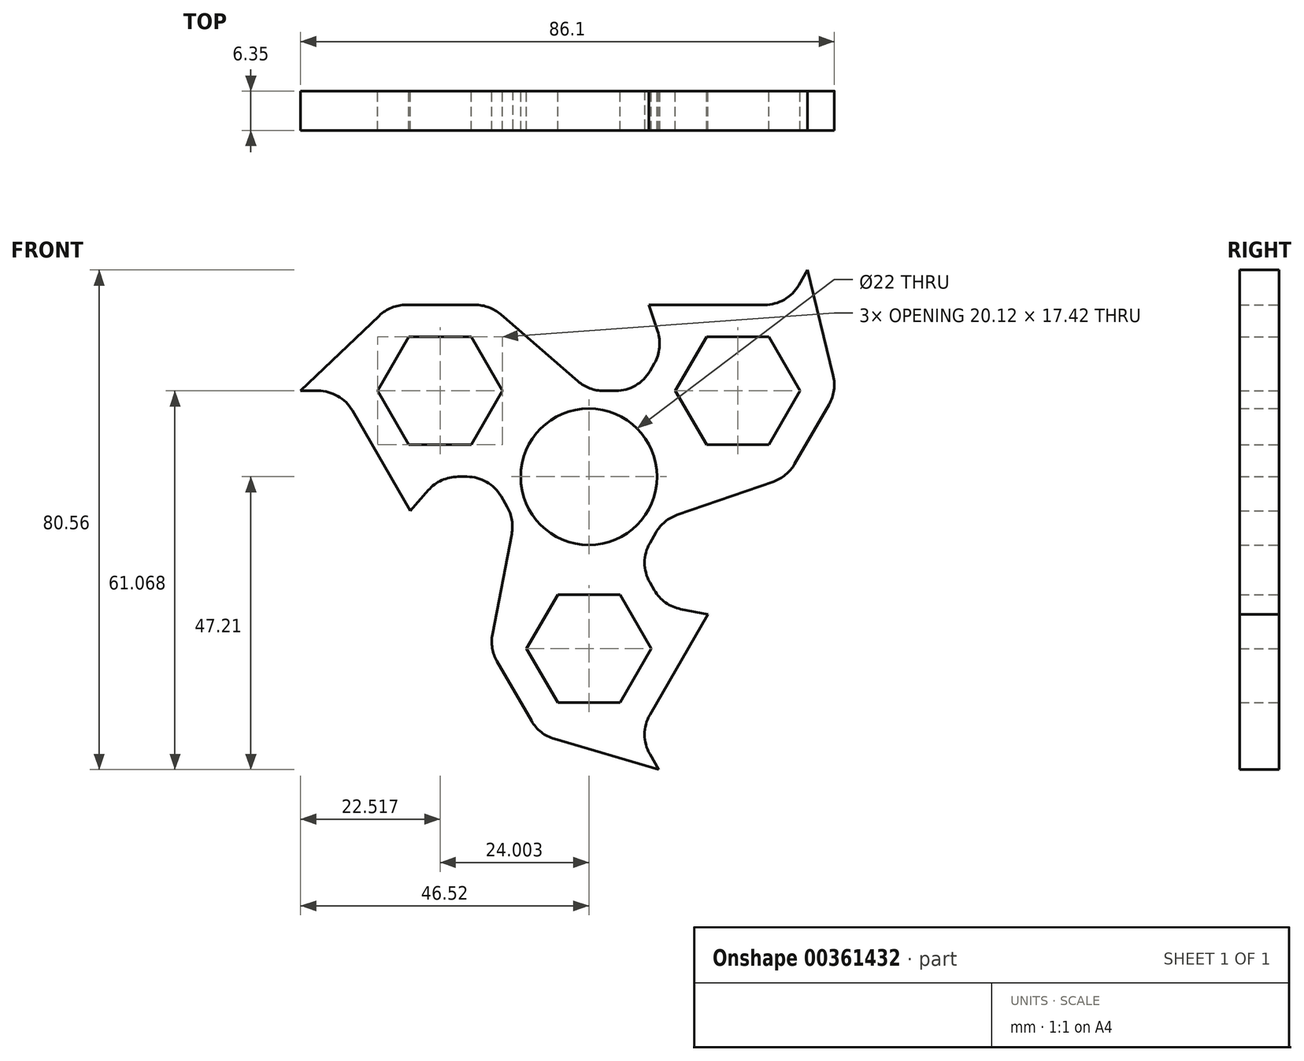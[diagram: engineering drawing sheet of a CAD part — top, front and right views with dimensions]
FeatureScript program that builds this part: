
annotation { "Feature Type Name" : "Feature", "Feature Type Description" : "" }
export const myFeature = defineFeature(function(context is Context, id is Id, definition is map)
    precondition{}
    {
        {
            var Q0;
            Q0=qCreatedBy(makeId("Front.planeOp"),FACE);
            var sketch = newSketch(context, id + "F0", { "sketchPlane" : qUnion([Q0])});
            skCircle(sketch, "E0.cCircle", {"center": v(0, 0) * mm, "radius": 13.86 * mm, "construction": true});
            skLineSegment(sketch, "E0.0", {"start": v(8, -13.86) * mm, "end": v(-8, -13.86) * mm});
            skLineSegment(sketch, "E0.1", {"start": v(-8, -13.86) * mm, "end": v(-16, 0) * mm});
            skLineSegment(sketch, "E0.2", {"start": v(-16, 0) * mm, "end": v(-8, 13.86) * mm});
            skLineSegment(sketch, "E0.3", {"start": v(-8, 13.86) * mm, "end": v(8, 13.86) * mm});
            skLineSegment(sketch, "E0.4", {"start": v(8, 13.86) * mm, "end": v(16, 0) * mm});
            skLineSegment(sketch, "E0.5", {"start": v(16, 0) * mm, "end": v(8, -13.86) * mm});
            skPoint(sketch, "E0.0.midPoint", {"position": v(0, -13.86) * mm});
            skCircle(sketch, "E1.cCircle", {"center": v(-24, 13.86) * mm, "radius": 13.86 * mm, "construction": true});
            skLineSegment(sketch, "E1.0", {"start": v(-16, 0) * mm, "end": v(-32, 0) * mm});
            skLineSegment(sketch, "E1.1", {"start": v(-32, 0) * mm, "end": v(-40, 13.86) * mm});
            skLineSegment(sketch, "E1.2", {"start": v(-40, 13.86) * mm, "end": v(-32, 27.72) * mm});
            skLineSegment(sketch, "E1.3", {"start": v(-32, 27.72) * mm, "end": v(-16, 27.72) * mm});
            skLineSegment(sketch, "E1.4", {"start": v(-16, 27.72) * mm, "end": v(-8, 13.86) * mm});
            skLineSegment(sketch, "E1.5", {"start": v(-8, 13.86) * mm, "end": v(-16, 0) * mm});
            skPoint(sketch, "E1.0.midPoint", {"position": v(-24, 0) * mm});
            skCircle(sketch, "E2", {"center": v(0, 0) * mm, "radius": 11 * mm});
            skCircle(sketch, "E3.cCircle", {"center": v(-24, 13.86) * mm, "radius": 8.71 * mm, "construction": true});
            skLineSegment(sketch, "E3.0", {"start": v(-18.97, 5.15) * mm, "end": v(-29.03, 5.15) * mm});
            skLineSegment(sketch, "E3.1", {"start": v(-29.03, 5.15) * mm, "end": v(-34.06, 13.86) * mm});
            skLineSegment(sketch, "E3.2", {"start": v(-34.06, 13.86) * mm, "end": v(-29.03, 22.57) * mm});
            skLineSegment(sketch, "E3.3", {"start": v(-29.03, 22.57) * mm, "end": v(-18.97, 22.57) * mm});
            skLineSegment(sketch, "E3.4", {"start": v(-18.97, 22.57) * mm, "end": v(-13.94, 13.86) * mm});
            skLineSegment(sketch, "E3.5", {"start": v(-13.94, 13.86) * mm, "end": v(-18.97, 5.15) * mm});
            skPoint(sketch, "E3.0.midPoint", {"position": v(-24, 5.15) * mm});
            skLineSegment(sketch, "E4.1.2", {"start": v(8, -41.57) * mm, "end": v(-8, -41.57) * mm});
            skCircle(sketch, "E4.1.3", {"center": v(0, -27.72) * mm, "radius": 13.86 * mm, "construction": true});
            skLineSegment(sketch, "E4.1.4", {"start": v(-16, -27.72) * mm, "end": v(-8, -13.86) * mm});
            skLineSegment(sketch, "E4.1.6", {"start": v(8, -13.86) * mm, "end": v(16, -27.72) * mm});
            skLineSegment(sketch, "E4.1.7", {"start": v(-5.03, -36.43) * mm, "end": v(-10.06, -27.72) * mm});
            skCircle(sketch, "E4.1.8", {"center": v(0, -27.72) * mm, "radius": 8.71 * mm, "construction": true});
            skLineSegment(sketch, "E4.1.9", {"start": v(5.03, -36.43) * mm, "end": v(-5.03, -36.43) * mm});
            skLineSegment(sketch, "E4.1.10", {"start": v(10.06, -27.72) * mm, "end": v(5.03, -36.43) * mm});
            skLineSegment(sketch, "E4.1.11", {"start": v(5.03, -19) * mm, "end": v(10.06, -27.72) * mm});
            skLineSegment(sketch, "E4.1.12", {"start": v(-5.03, -19) * mm, "end": v(5.03, -19) * mm});
            skLineSegment(sketch, "E4.2.2", {"start": v(32, 27.72) * mm, "end": v(40, 13.86) * mm});
            skCircle(sketch, "E4.2.3", {"center": v(24, 13.86) * mm, "radius": 13.86 * mm, "construction": true});
            skLineSegment(sketch, "E4.2.4", {"start": v(32, 0) * mm, "end": v(16, 0) * mm});
            skLineSegment(sketch, "E4.2.6", {"start": v(8, 13.86) * mm, "end": v(16, 27.72) * mm});
            skLineSegment(sketch, "E4.2.7", {"start": v(34.06, 13.86) * mm, "end": v(29.03, 5.15) * mm});
            skCircle(sketch, "E4.2.8", {"center": v(24, 13.86) * mm, "radius": 8.71 * mm, "construction": true});
            skLineSegment(sketch, "E4.2.9", {"start": v(29.03, 22.57) * mm, "end": v(34.06, 13.86) * mm});
            skLineSegment(sketch, "E4.2.10", {"start": v(18.97, 22.57) * mm, "end": v(29.03, 22.57) * mm});
            skLineSegment(sketch, "E4.2.11", {"start": v(13.94, 13.86) * mm, "end": v(18.97, 22.57) * mm});
            skLineSegment(sketch, "E4.2.12", {"start": v(18.97, 5.15) * mm, "end": v(13.94, 13.86) * mm});
            skLineSegment(sketch, "E5", {"start": v(-32, 0) * mm, "end": v(-28.83, -5.5) * mm});
            skLineSegment(sketch, "E6", {"start": v(-28.83, -5.5) * mm, "end": v(-24, 0) * mm});
            skLineSegment(sketch, "E7.1.0", {"start": v(16, -27.72) * mm, "end": v(19.18, -22.22) * mm});
            skLineSegment(sketch, "E7.1.1", {"start": v(19.18, -22.22) * mm, "end": v(12, -20.79) * mm});
            skLineSegment(sketch, "E7.2.0", {"start": v(16, 27.72) * mm, "end": v(9.65, 27.72) * mm});
            skLineSegment(sketch, "E7.2.1", {"start": v(9.65, 27.72) * mm, "end": v(12, 20.79) * mm});
            skLineSegment(sketch, "E8.1.0", {"start": v(-10.06, -27.72) * mm, "end": v(-5.03, -19) * mm});
            skLineSegment(sketch, "E8.2.0", {"start": v(29.03, 5.15) * mm, "end": v(18.97, 5.15) * mm});
            skLineSegment(sketch, "E9", {"start": v(16, 27.72) * mm, "end": v(32, 27.72) * mm});
            skLineSegment(sketch, "E10", {"start": v(40, 13.86) * mm, "end": v(32, 0) * mm});
            skLineSegment(sketch, "E11", {"start": v(16, -27.72) * mm, "end": v(8, -41.57) * mm});
            skLineSegment(sketch, "E12", {"start": v(-8, -41.57) * mm, "end": v(-16, -27.72) * mm});
            skLineSegment(sketch, "E13", {"start": v(-32, 27.72) * mm, "end": v(-46.52, 13.86) * mm});
            skLineSegment(sketch, "E14", {"start": v(-46.52, 13.86) * mm, "end": v(-40, 13.86) * mm});
            skLineSegment(sketch, "E15.1.0", {"start": v(-8, -41.57) * mm, "end": v(11.26, -47.21) * mm});
            skLineSegment(sketch, "E15.1.1", {"start": v(11.26, -47.21) * mm, "end": v(8, -41.57) * mm});
            skLineSegment(sketch, "E15.2.0", {"start": v(40, 13.86) * mm, "end": v(35.26, 33.35) * mm});
            skLineSegment(sketch, "E15.2.1", {"start": v(35.26, 33.35) * mm, "end": v(32, 27.72) * mm});
            skLineSegment(sketch, "E16", {"start": v(-16, 27.72) * mm, "end": v(0, 13.86) * mm});
            skLineSegment(sketch, "E17.1.0", {"start": v(-16, -27.72) * mm, "end": v(-12, -6.93) * mm});
            skLineSegment(sketch, "E17.2.0", {"start": v(32, 0) * mm, "end": v(12, -6.93) * mm});
            skSolve(sketch);
        }
        {
            var Q0;
            {var subQ5=sQuery(id+"F0.wireOp",EDGE,"E1.2");Q0=makeQuery(id+"F0.imprint","IMPRINT",FACE,{"disambiguationData":[TD([[makeQuery(id+"F0.imprint","IMPRINT",EDGE,{"derivedFrom":subQ5}),-1.0]])]});}
            var Q1;
            {var subQ0=sQuery(id+"F0.wireOp",EDGE,"E5");Q1=makeQuery(id+"F0.imprint","IMPRINT",FACE,{"disambiguationData":[TD([[makeQuery(id+"F0.imprint","IMPRINT",EDGE,{"derivedFrom":subQ0}),1.0]])]});}
            var Q2;
            Q2=makeQuery(id+"F0.imprint","IMPRINT",FACE,{"disambiguationData":[TD([[makeQuery(id+"F0.imprint","IMPRINT",EDGE,{"derivedFrom":sQuery(id+"F0.wireOp",EDGE,"E0.1")}),-1.0]])]});
            var Q3;
            {var subQ7=sQuery(id+"F0.wireOp",EDGE,"E4.2.2");Q3=makeQuery(id+"F0.imprint","IMPRINT",FACE,{"disambiguationData":[TD([[makeQuery(id+"F0.imprint","IMPRINT",EDGE,{"derivedFrom":subQ7}),-1.0]])]});}
            var Q4;
            {var subQ0=sQuery(id+"F0.wireOp",EDGE,"E7.2.0");Q4=makeQuery(id+"F0.imprint","IMPRINT",FACE,{"disambiguationData":[TD([[makeQuery(id+"F0.imprint","IMPRINT",EDGE,{"derivedFrom":subQ0}),1.0]])]});}
            var Q5;
            {var subQ7=sQuery(id+"F0.wireOp",EDGE,"E4.1.2");Q5=makeQuery(id+"F0.imprint","IMPRINT",FACE,{"disambiguationData":[TD([[makeQuery(id+"F0.imprint","IMPRINT",EDGE,{"derivedFrom":subQ7}),-1.0]])]});}
            var Q6;
            {var subQ0=sQuery(id+"F0.wireOp",EDGE,"E7.1.0");Q6=makeQuery(id+"F0.imprint","IMPRINT",FACE,{"disambiguationData":[TD([[makeQuery(id+"F0.imprint","IMPRINT",EDGE,{"derivedFrom":subQ0}),1.0]])]});}
            var Q7;
            Q7=makeQuery(id+"F0.imprint","IMPRINT",FACE,{"disambiguationData":[TD([[makeQuery(id+"F0.imprint","IMPRINT",EDGE,{"derivedFrom":sQuery(id+"F0.wireOp",EDGE,"E1.2")}),1.0]])]});
            var Q8;
            Q8=makeQuery(id+"F0.imprint","IMPRINT",FACE,{"disambiguationData":[TD([[makeQuery(id+"F0.imprint","IMPRINT",EDGE,{"derivedFrom":sQuery(id+"F0.wireOp",EDGE,"E4.2.2")}),1.0]])]});
            var Q9;
            Q9=makeQuery(id+"F0.imprint","IMPRINT",FACE,{"disambiguationData":[TD([[makeQuery(id+"F0.imprint","IMPRINT",EDGE,{"derivedFrom":sQuery(id+"F0.wireOp",EDGE,"E4.1.2")}),1.0]])]});
            var Q10;
            {var subQ0=sQuery(id+"F0.wireOp",EDGE,"E1.4");Q10=makeQuery(id+"F0.imprint","IMPRINT",FACE,{"disambiguationData":[TD([[makeQuery(id+"F0.imprint","IMPRINT",EDGE,{"derivedFrom":subQ0}),1.0]])]});}
            var Q11;
            {var subQ0=sQuery(id+"F0.wireOp",EDGE,"E4.1.4");Q11=makeQuery(id+"F0.imprint","IMPRINT",FACE,{"disambiguationData":[TD([[makeQuery(id+"F0.imprint","IMPRINT",EDGE,{"derivedFrom":subQ0}),1.0]])]});}
            var Q12;
            {var subQ0=sQuery(id+"F0.wireOp",EDGE,"E4.2.4");Q12=makeQuery(id+"F0.imprint","IMPRINT",FACE,{"disambiguationData":[TD([[makeQuery(id+"F0.imprint","IMPRINT",EDGE,{"derivedFrom":subQ0}),1.0]])]});}
            extrude(context, id + "F1", {"entities" : qUnion([Q0, Q1, Q2, Q3, Q4, Q5, Q6, Q7, Q8, Q9, Q10, Q11, Q12]), "depth" : 6.35 * mm, "offsetDistance" : 25.4 * mm});
        }
        {
            var Q0;
            Q0=makeQuery(id+"F1.opExtrude","SWEPT_EDGE",EDGE,{"disambiguationData":[OSD([sQuery(id+"F0.wireOp",EDGE,"E4.2.2"),sQuery(id+"F0.wireOp",EDGE,"E9"),sQuery(id+"F0.wireOp",EDGE,"E15.2.1")])]});
            var Q1;
            Q1=makeQuery(id+"F1.opExtrude","SWEPT_EDGE",EDGE,{"disambiguationData":[OSD([sQuery(id+"F0.wireOp",EDGE,"E0.3"),sQuery(id+"F0.wireOp",EDGE,"E0.4"),sQuery(id+"F0.wireOp",EDGE,"E4.2.6")])]});
            var Q2;
            Q2=makeQuery(id+"F1.opExtrude","SWEPT_EDGE",EDGE,{"disambiguationData":[OSD([sQuery(id+"F0.wireOp",EDGE,"E0.3"),sQuery(id+"F0.wireOp",EDGE,"E16")])]});
            var Q3;
            Q3=makeQuery(id+"F1.opExtrude","SWEPT_EDGE",EDGE,{"disambiguationData":[OSD([sQuery(id+"F0.wireOp",EDGE,"E1.3"),sQuery(id+"F0.wireOp",EDGE,"E1.4"),sQuery(id+"F0.wireOp",EDGE,"E16")])]});
            var Q4;
            Q4=makeQuery(id+"F1.opExtrude","SWEPT_EDGE",EDGE,{"disambiguationData":[OSD([sQuery(id+"F0.wireOp",EDGE,"E1.2"),sQuery(id+"F0.wireOp",EDGE,"E1.3"),sQuery(id+"F0.wireOp",EDGE,"E13")])]});
            var Q5;
            Q5=makeQuery(id+"F1.opExtrude","SWEPT_EDGE",EDGE,{"disambiguationData":[OSD([sQuery(id+"F0.wireOp",EDGE,"E1.1"),sQuery(id+"F0.wireOp",EDGE,"E1.2"),sQuery(id+"F0.wireOp",EDGE,"E14")])]});
            var Q6;
            Q6=makeQuery(id+"F1.opExtrude","SWEPT_EDGE",EDGE,{"disambiguationData":[OSD([sQuery(id+"F0.wireOp",EDGE,"E0.1"),sQuery(id+"F0.wireOp",EDGE,"E1.0"),sQuery(id+"F0.wireOp",EDGE,"E1.5")])]});
            var Q7;
            Q7=makeQuery(id+"F1.opExtrude","SWEPT_EDGE",EDGE,{"disambiguationData":[OSD([sQuery(id+"F0.wireOp",EDGE,"E0.1"),sQuery(id+"F0.wireOp",EDGE,"E17.1.0")])]});
            var Q8;
            Q8=makeQuery(id+"F1.opExtrude","SWEPT_EDGE",EDGE,{"disambiguationData":[OSD([sQuery(id+"F0.wireOp",EDGE,"E4.1.4"),sQuery(id+"F0.wireOp",EDGE,"E12"),sQuery(id+"F0.wireOp",EDGE,"E17.1.0")])]});
            var Q9;
            Q9=makeQuery(id+"F1.opExtrude","SWEPT_EDGE",EDGE,{"disambiguationData":[OSD([sQuery(id+"F0.wireOp",EDGE,"E4.1.2"),sQuery(id+"F0.wireOp",EDGE,"E12"),sQuery(id+"F0.wireOp",EDGE,"E15.1.0")])]});
            var Q10;
            Q10=makeQuery(id+"F1.opExtrude","SWEPT_EDGE",EDGE,{"disambiguationData":[OSD([sQuery(id+"F0.wireOp",EDGE,"E4.1.2"),sQuery(id+"F0.wireOp",EDGE,"E11"),sQuery(id+"F0.wireOp",EDGE,"E15.1.1")])]});
            var Q11;
            Q11=makeQuery(id+"F1.opExtrude","SWEPT_EDGE",EDGE,{"disambiguationData":[OSD([sQuery(id+"F0.wireOp",EDGE,"E0.5"),sQuery(id+"F0.wireOp",EDGE,"E0.0"),sQuery(id+"F0.wireOp",EDGE,"E4.1.6")])]});
            var Q12;
            Q12=makeQuery(id+"F1.opExtrude","SWEPT_EDGE",EDGE,{"disambiguationData":[OSD([sQuery(id+"F0.wireOp",EDGE,"E0.5"),sQuery(id+"F0.wireOp",EDGE,"E17.2.0")])]});
            var Q13;
            Q13=makeQuery(id+"F1.opExtrude","SWEPT_EDGE",EDGE,{"disambiguationData":[OSD([sQuery(id+"F0.wireOp",EDGE,"E4.2.4"),sQuery(id+"F0.wireOp",EDGE,"E10"),sQuery(id+"F0.wireOp",EDGE,"E17.2.0")])]});
            var Q14;
            Q14=makeQuery(id+"F1.opExtrude","SWEPT_EDGE",EDGE,{"disambiguationData":[OSD([sQuery(id+"F0.wireOp",EDGE,"E4.2.2"),sQuery(id+"F0.wireOp",EDGE,"E10"),sQuery(id+"F0.wireOp",EDGE,"E15.2.0")])]});
            var Q15;
            Q15=makeQuery(id+"F1.opExtrude","SWEPT_EDGE",EDGE,{"disambiguationData":[OSD([sQuery(id+"F0.wireOp",EDGE,"E1.0"),sQuery(id+"F0.wireOp",EDGE,"E6")])]});
            var Q16;
            Q16=makeQuery(id+"F1.opExtrude","SWEPT_EDGE",EDGE,{"disambiguationData":[OSD([sQuery(id+"F0.wireOp",EDGE,"E4.1.6"),sQuery(id+"F0.wireOp",EDGE,"E7.1.1")])]});
            var Q17;
            Q17=makeQuery(id+"F1.opExtrude","SWEPT_EDGE",EDGE,{"disambiguationData":[OSD([sQuery(id+"F0.wireOp",EDGE,"E4.2.6"),sQuery(id+"F0.wireOp",EDGE,"E7.2.1")])]});
            fillet(context, id + "F2", {"entities" : qUnion([Q0, Q1, Q2, Q3, Q4, Q5, Q6, Q7, Q8, Q9, Q10, Q11, Q12, Q13, Q14, Q15, Q16, Q17]), "radius" : 6.35 * mm, "tangentPropagation" : true, "allowEdgeOverflow" : false});
        }
    });
